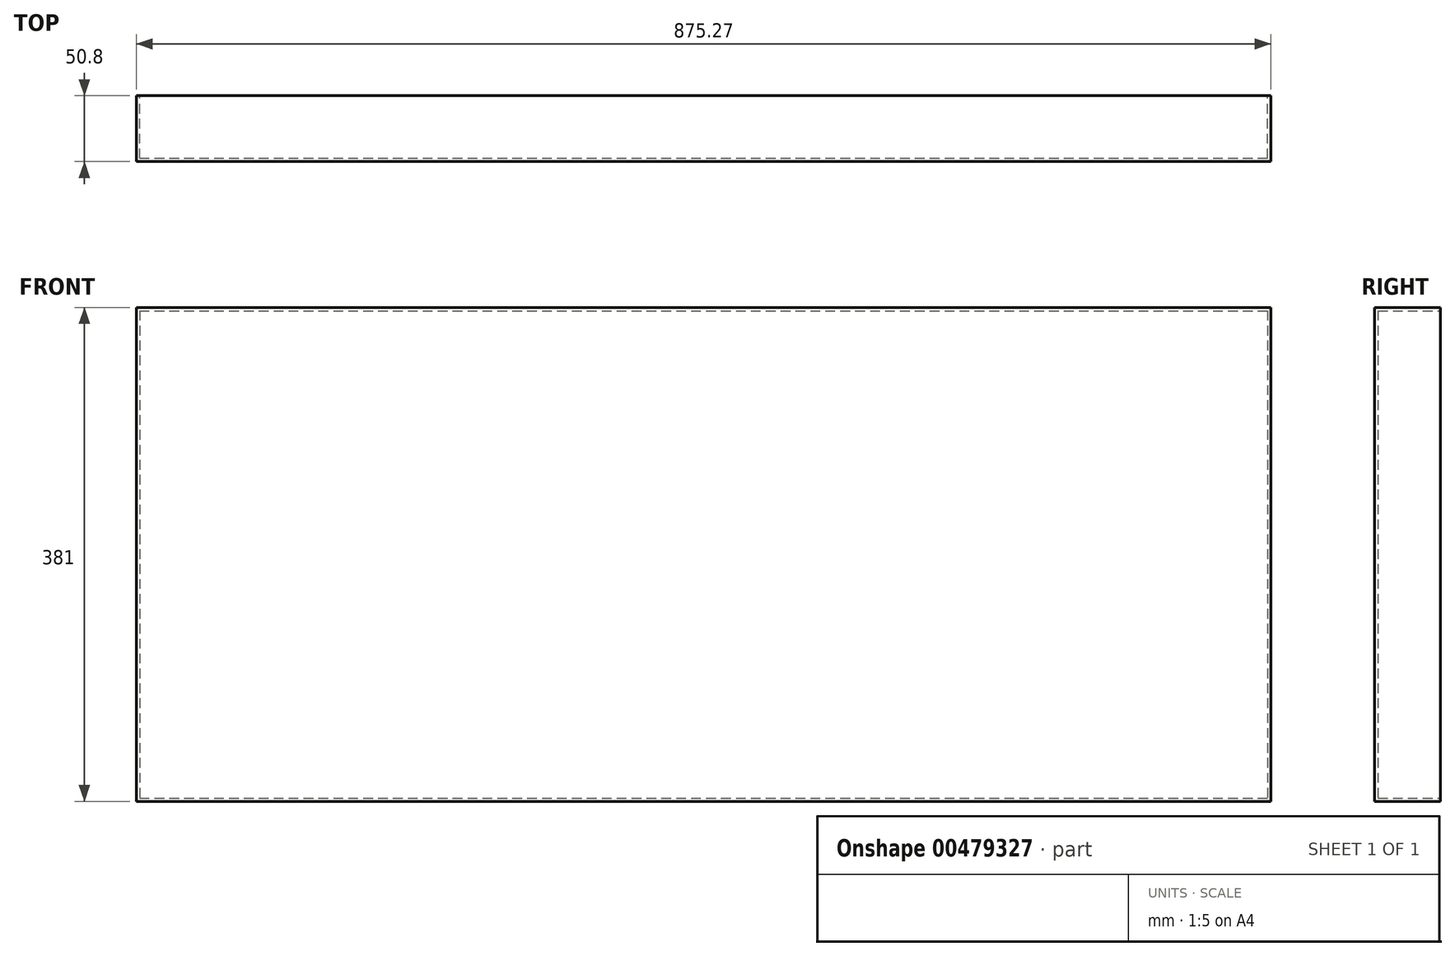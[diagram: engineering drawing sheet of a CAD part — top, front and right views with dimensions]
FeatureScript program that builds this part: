
annotation { "Feature Type Name" : "Feature", "Feature Type Description" : "" }
export const myFeature = defineFeature(function(context is Context, id is Id, definition is map)
    precondition{}
    {
        {
            var Q0;
            Q0=qCreatedBy(makeId("Front.planeOp"),FACE);
            var sketch = newSketch(context, id + "F0", { "sketchPlane" : qUnion([Q0])});
            skLineSegment(sketch, "E0.bottom", {"start": v(-432.4, 194.5) * mm, "end": v(442.86, 194.5) * mm});
            skLineSegment(sketch, "E0.top", {"start": v(-432.4, -186.5) * mm, "end": v(442.86, -186.5) * mm});
            skLineSegment(sketch, "E0.left", {"start": v(-432.4, 194.5) * mm, "end": v(-432.4, -186.5) * mm});
            skLineSegment(sketch, "E0.right", {"start": v(442.86, 194.5) * mm, "end": v(442.86, -186.5) * mm});
            skSolve(sketch);
        }
        {
            var Q0;
            Q0 = qSketchRegion(id + "F0", true);
            extrude(context, id + "F1", {"entities" : qUnion([Q0]), "depth" : 50.8 * mm});
        }
        {
            var Q0;
            Q0=makeQuery(id+"F1.opExtrude","CAP_FACE",FACE,{"disambiguationData":[OSD([sQuery(id+"F0.wireOp",EDGE,"E0.bottom"),sQuery(id+"F0.wireOp",EDGE,"E0.top"),sQuery(id+"F0.wireOp",EDGE,"E0.left"),sQuery(id+"F0.wireOp",EDGE,"E0.right")])],"isStart":true});
            shell(context, id + "F2", {"entities" : qUnion([Q0]), "thickness" : 2.54 * mm});
        }
    });
